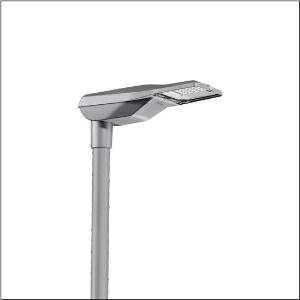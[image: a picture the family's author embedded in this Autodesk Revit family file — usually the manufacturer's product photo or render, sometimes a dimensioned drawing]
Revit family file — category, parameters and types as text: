
# Revit family: streetlight_sl_21_iq_micro___stw1_0a_5xe1e61d08cb_4749
name_source: partatom
category: Lighting Fixtures
units: mm (PartAtom-declared; Revit-internal decimal feet)

## family parameters
Cut with Voids When Loaded = No
Host = Face
Light Source = No
Part Type = Normal
Room Calculation Point = No
Round Connector Dimension = Use Diameter
Shared = No

## types (1)
- --- (1 x LED, 2570 lm, 19.4 W, 2700K)
    Apparent Load = 19 VA
    CIE Flux Codes = 38 75 98 100 100
    Color Rendering = 70
    Color Temperature = 2700K
    Default Elevation = 1800 mm
    Description = Streetlight SL 21 iQ micro, mast luminaire, primary light control with lens, of PMMA, primary optical cover: cover, of toughened safety glass, transparent, light distribution: STW1.0a, light emission: direct distribution, primary light characteristic: asymmetric, installation type: post-top, side-entry, LED, High Power LED, rated luminous flux: 2.570lm, luminous efficacy: 133lm/W, light colour: 727, colour temperature: 2700K, control: Auto-Match, Temp-Guard, Lumen-Switch, Night-Set, Smart-Wire, Light-Fading, Desk-Remote (wireless, voltage-free reading and setting of iQ features in the workshop via application-optimized NFC function/RFID function), optimised constant luminous flux control (CLO 2.0), presetting dimming linear, mains connection: 220..240V, AC, 50/60Hz, start of lifetime: 19W, end of service life: 20W, reduction: 10W, luminaire housing, of diecast aluminium, powder-coated, Siteco® metallic grey (DB 702S), corrosivity category C5 mid according to DIN EN ISO 12944, please order mast flange separately, inclination adjustable: 0°, 5°, 10°, 15°, sealing non-destructively replaceable, multi-level sealing system, length: 528mm, width: 235mm, height: 110mm, mast flange for spigot size: 42mm (side-entry): 5XC10008XM4, 60/48mm (side-entry/post-top): 5XC10108XM2, 76/60mm (side-entry/post-top): 5XC10108XM1, protection rating (complete): IP66, insulation class (complete): insulation class II (safety insulation), certification: CE, ENEC, ENEC+, VDE, impact resistance: IK09, permissible operating ambient temperature for outdoor applications: -40..+50°C, standard-compliant lighting for roads and squares, packaging unit: 1 piece

Light Distribution: STW1.0a
    Height = 110 mm
    Lamp = 1 x LED
    Lamp Light Flux = 2570 lm
    Lamp Power = 19.4 W
    Lamp count = 1
    Length = 528 mm
    Luminous efficacy = 132 lm/W
    Manufacturer = Siteco
    ModVariant = No
    Model = 5XE1E61D08CB
    Number of Poles = 1
    OnlyDefault = Yes
    Power Factor = 1
    Product Name = Streetlight SL 21 iQ micro | STW1.0a
    Product group = mast luminaire | pylon top
    ProductGroupID = 6100
    Protection Class = Protection class II
    Protection Degree = IP 66
    RLX_Detail_Level = 1
    RLX_Emergency_Light_Flux = 0 lm
    RLX_Emergency_Type = 0
    RLX_Emergency_Type_DB = No
    RlxData = <blob elided: 98765 chars, md5=14428e86>
    Socket = socket
    Standby Power = 0 W
    System Light Flux = 2570 lm
    System Power = 19 W
    Type Comments = factory setting: luminous flux: 100 % | dim-lin: 254 | 387 mA
    Type Image = l_1006881.jpg
    URL = http://relux.com
    VarID = @adj_088121
    Voltage = 0 V
    Weight = 0.00 kg
    Width = 235 mm

## geometry (parser evidence)
native form markers: Blend x4, Sweep x9
no freeform markers — native parametric forms only
